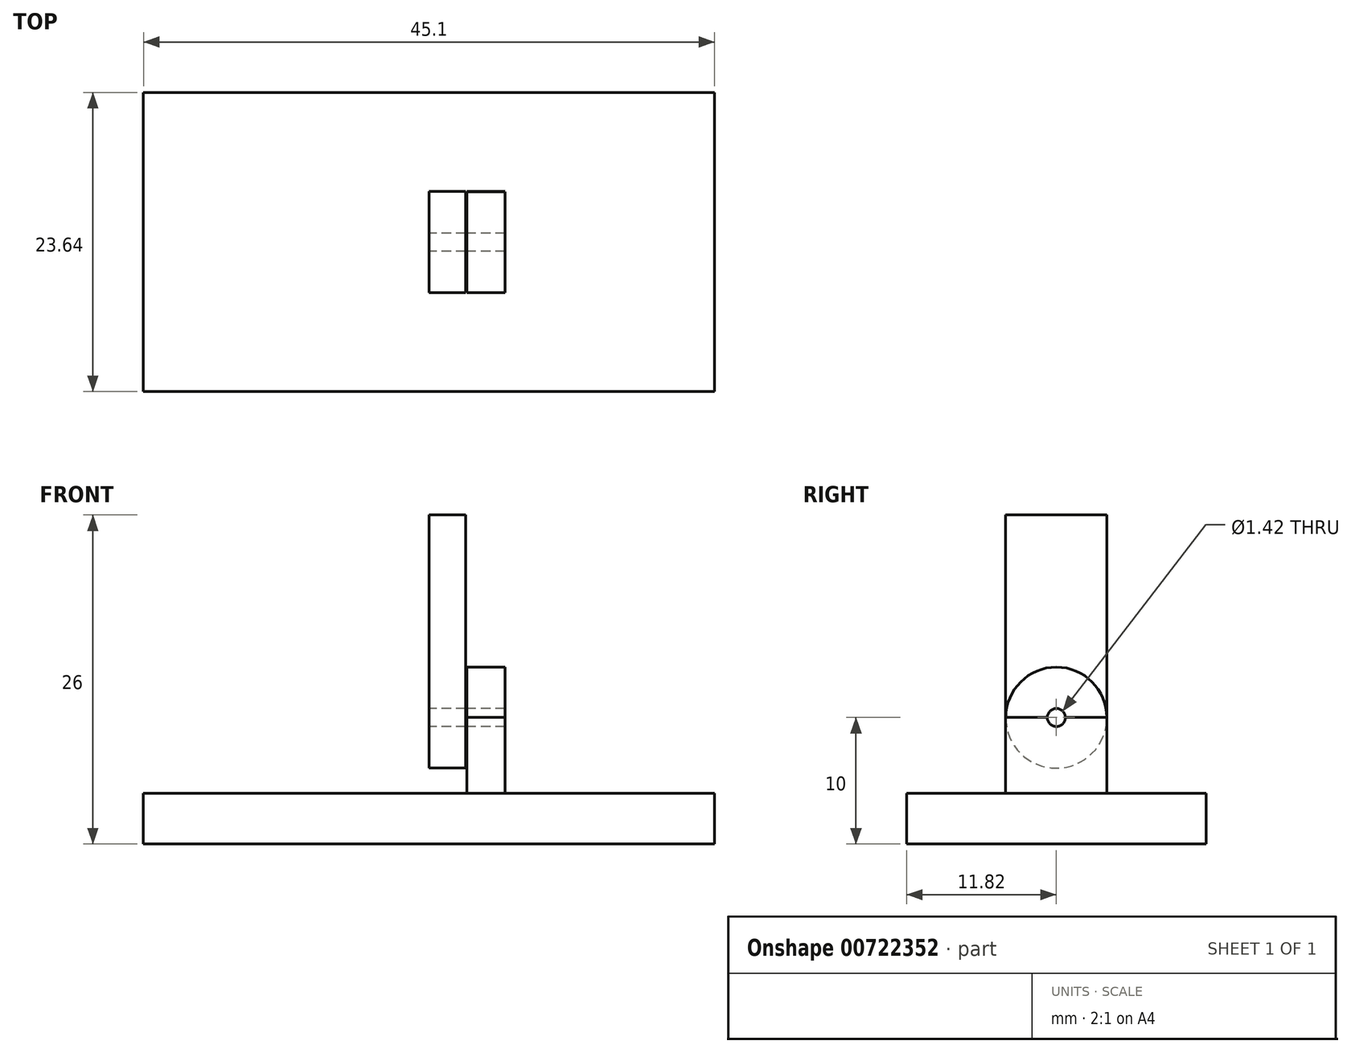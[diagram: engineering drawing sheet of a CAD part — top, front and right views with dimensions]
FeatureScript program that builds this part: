
annotation { "Feature Type Name" : "Feature", "Feature Type Description" : "" }
export const myFeature = defineFeature(function(context is Context, id is Id, definition is map)
    precondition{}
    {
        {
            var Q0;
            Q0=qCreatedBy(makeId("Top.planeOp"),FACE);
            var sketch = newSketch(context, id + "F0", { "sketchPlane" : qUnion([Q0])});
            skLineSegment(sketch, "E0.bottom", {"start": v(22.55, -11.82) * mm, "end": v(-22.55, -11.82) * mm});
            skLineSegment(sketch, "E0.top", {"start": v(22.55, 11.82) * mm, "end": v(-22.55, 11.82) * mm});
            skLineSegment(sketch, "E0.left", {"start": v(22.55, -11.82) * mm, "end": v(22.55, 11.82) * mm});
            skLineSegment(sketch, "E0.right", {"start": v(-22.55, -11.82) * mm, "end": v(-22.55, 11.82) * mm});
            skPoint(sketch, "E0.middle", {"position": v(0, 0) * mm});
            skSolve(sketch);
        }
        {
            var Q0;
            Q0 = qSketchRegion(id + "F0", true);
            extrude(context, id + "F1", {"entities" : qUnion([Q0]), "depth" : 4 * mm, "offsetDistance" : 25 * mm});
        }
        {
            var Q0;
            Q0=makeQuery(id+"F1.opExtrude","CAP_FACE",FACE,{"disambiguationData":[OSD([sQuery(id+"F0.wireOp",EDGE,"E0.bottom"),sQuery(id+"F0.wireOp",EDGE,"E0.top"),sQuery(id+"F0.wireOp",EDGE,"E0.left"),sQuery(id+"F0.wireOp",EDGE,"E0.right")])],"isStart":false});
            var sketch = newSketch(context, id + "F2", { "sketchPlane" : qUnion([Q0])});
            skLineSegment(sketch, "E1.bottom", {"start": v(3, 4) * mm, "end": v(6, 4) * mm});
            skLineSegment(sketch, "E1.top", {"start": v(3, -4) * mm, "end": v(6, -4) * mm});
            skLineSegment(sketch, "E1.left", {"start": v(3, 4) * mm, "end": v(3, -4) * mm});
            skLineSegment(sketch, "E1.right", {"start": v(6, 4) * mm, "end": v(6, -4) * mm});
            skSolve(sketch);
        }
        {
            var Q0;
            Q0=makeQuery(id+"F2.imprint","IMPRINT",FACE,{"disambiguationData":[TD([[makeQuery(id+"F2.imprint","IMPRINT",EDGE,{"derivedFrom":sQuery(id+"F2.wireOp",EDGE,"E1.bottom")}),-1.0]])]});
            extrude(context, id + "F3", {"entities" : qUnion([Q0]), "operationType" : NewBodyOperationType.ADD, "depth" : 6 * mm, "offsetDistance" : 25 * mm});
        }
        {
            var Q0;
            Q0=makeQuery(id+"F3.opExtrude","SWEPT_FACE",FACE,{"disambiguationData":[OSD([sQuery(id+"F2.wireOp",EDGE,"E1.right")])]});
            var sketch = newSketch(context, id + "F4", { "sketchPlane" : qUnion([Q0])});
            skCircle(sketch, "E2", {"center": v(0, 10) * mm, "radius": 3.99 * mm});
            skCircle(sketch, "E3", {"center": v(0, 10) * mm, "radius": 0.48 * mm});
            skSolve(sketch);
        }
        {
            var Q0;
            {var subQ0=sQuery(id+"F4.wireOp",EDGE,"E2");var subQ1=makeQuery(id+"F3.opExtrude","CAP_EDGE",EDGE,{"disambiguationData":[OSD([sQuery(id+"F2.wireOp",EDGE,"E1.right")])],"isStart":false});var subQ2=makeQuery(id+"F4.imprint","INTERSECT",VERTEX,{"disambiguationData":[OD(0.0)],"derivedFrom":[subQ1,subQ0]});Q0=makeQuery(id+"F4.imprint","IMPRINT",FACE,{"disambiguationData":[TD([[makeQuery(id+"F4.imprint","IMPRINT",EDGE,{"disambiguationData":[TD([[subQ2,-1.0]])],"derivedFrom":subQ0}),1.0]])]});}
            extrude(context, id + "F5", {"entities" : qUnion([Q0]), "oppositeDirection" : true, "depth" : 3 * mm, "offsetDistance" : 25 * mm});
        }
        {
            var Q0;
            {var subQ0=sQuery(id+"F4.wireOp",EDGE,"E3");var subQ1=makeQuery(id+"F3.opExtrude","CAP_EDGE",EDGE,{"disambiguationData":[OSD([sQuery(id+"F2.wireOp",EDGE,"E1.right")])],"isStart":false});var subQ2=makeQuery(id+"F4.imprint","INTERSECT",VERTEX,{"disambiguationData":[OD(0.0)],"derivedFrom":[subQ1,subQ0]});Q0=makeQuery(id+"F4.imprint","IMPRINT",FACE,{"disambiguationData":[TD([[makeQuery(id+"F4.imprint","IMPRINT",EDGE,{"disambiguationData":[TD([[subQ2,1.0]])],"derivedFrom":subQ0}),1.0]])]});}
            extrude(context, id + "F6", {"entities" : qUnion([Q0]), "operationType" : NewBodyOperationType.REMOVE, "oppositeDirection" : true, "depth" : 4 * mm, "offsetDistance" : 25 * mm});
        }
        {
            var Q0;
            Q0=makeQuery(id+"F3.opExtrude","SWEPT_FACE",FACE,{"disambiguationData":[OSD([sQuery(id+"F2.wireOp",EDGE,"E1.top")])]});
            var sketch = newSketch(context, id + "F7", { "sketchPlane" : qUnion([Q0])});
            skLineSegment(sketch, "E4.bottom", {"start": v(0, 10) * mm, "end": v(2.9, 10) * mm});
            skLineSegment(sketch, "E4.top", {"start": v(0, 26) * mm, "end": v(2.9, 26) * mm});
            skLineSegment(sketch, "E4.left", {"start": v(0, 10) * mm, "end": v(0, 26) * mm});
            skLineSegment(sketch, "E4.right", {"start": v(2.9, 10) * mm, "end": v(2.9, 26) * mm});
            skSolve(sketch);
        }
        {
            var Q0;
            Q0=makeQuery(id+"F7.imprint","IMPRINT",FACE,{"disambiguationData":[TD([[makeQuery(id+"F7.imprint","IMPRINT",EDGE,{"derivedFrom":sQuery(id+"F7.wireOp",EDGE,"E4.bottom")}),1.0]])]});
            extrude(context, id + "F8", {"entities" : qUnion([Q0]), "oppositeDirection" : true, "depth" : 8 * mm, "offsetDistance" : 25 * mm});
        }
        {
            var Q0;
            Q0=makeQuery(id+"F8.opExtrude","SWEPT_FACE",FACE,{"disambiguationData":[OSD([sQuery(id+"F7.wireOp",EDGE,"E4.left")])]});
            var sketch = newSketch(context, id + "F9", { "sketchPlane" : qUnion([Q0])});
            skCircle(sketch, "E5", {"center": v(0, 10) * mm, "radius": 4 * mm});
            skCircle(sketch, "E6", {"center": v(0, 10) * mm, "radius": 0.71 * mm});
            skSolve(sketch);
        }
        {
            var Q0;
            {var subQ1=sQuery(id+"F7.wireOp",EDGE,"E4.left");var subQ2=makeQuery(id+"F8.opExtrude","SWEPT_EDGE",EDGE,{"disambiguationData":[OSD([sQuery(id+"F7.wireOp",EDGE,"E4.bottom"),subQ1])]});var subQ5=sQuery(id+"F9.wireOp",EDGE,"E6");var subQ6=makeQuery(id+"F9.imprint","INTERSECT",VERTEX,{"disambiguationData":[OD(0.0)],"derivedFrom":[subQ2,subQ5]});Q0=makeQuery(id+"F9.imprint","IMPRINT",FACE,{"disambiguationData":[TD([[makeQuery(id+"F9.imprint","IMPRINT",EDGE,{"disambiguationData":[TD([[subQ6,1.0]])],"derivedFrom":subQ5}),-1.0]])]});}
            extrude(context, id + "F10", {"entities" : qUnion([Q0]), "operationType" : NewBodyOperationType.ADD, "oppositeDirection" : true, "depth" : 2.9 * mm, "offsetDistance" : 25 * mm});
        }
        {
            var Q0;
            {var subQ0=sQuery(id+"F9.wireOp",EDGE,"E6");var subQ1=makeQuery(id+"F8.opExtrude","SWEPT_EDGE",EDGE,{"disambiguationData":[OSD([sQuery(id+"F7.wireOp",EDGE,"E4.bottom"),sQuery(id+"F7.wireOp",EDGE,"E4.left")])]});var subQ2=makeQuery(id+"F9.imprint","INTERSECT",VERTEX,{"disambiguationData":[OD(0.0)],"derivedFrom":[subQ1,subQ0]});Q0=makeQuery(id+"F9.imprint","IMPRINT",FACE,{"disambiguationData":[TD([[makeQuery(id+"F9.imprint","IMPRINT",EDGE,{"disambiguationData":[TD([[subQ2,-1.0]])],"derivedFrom":subQ0}),1.0]])]});}
            var Q1;
            {var subQ0=sQuery(id+"F9.wireOp",EDGE,"E6");var subQ1=makeQuery(id+"F8.opExtrude","SWEPT_EDGE",EDGE,{"disambiguationData":[OSD([sQuery(id+"F7.wireOp",EDGE,"E4.bottom"),sQuery(id+"F7.wireOp",EDGE,"E4.left")])]});var subQ2=makeQuery(id+"F9.imprint","INTERSECT",VERTEX,{"disambiguationData":[OD(0.0)],"derivedFrom":[subQ1,subQ0]});Q1=makeQuery(id+"F9.imprint","IMPRINT",FACE,{"disambiguationData":[TD([[makeQuery(id+"F9.imprint","IMPRINT",EDGE,{"disambiguationData":[TD([[subQ2,1.0]])],"derivedFrom":subQ0}),1.0]])]});}
            extrude(context, id + "F11", {"entities" : qUnion([Q0, Q1]), "operationType" : NewBodyOperationType.REMOVE, "oppositeDirection" : true, "depth" : 9 * mm, "offsetDistance" : 25 * mm});
        }
    });
